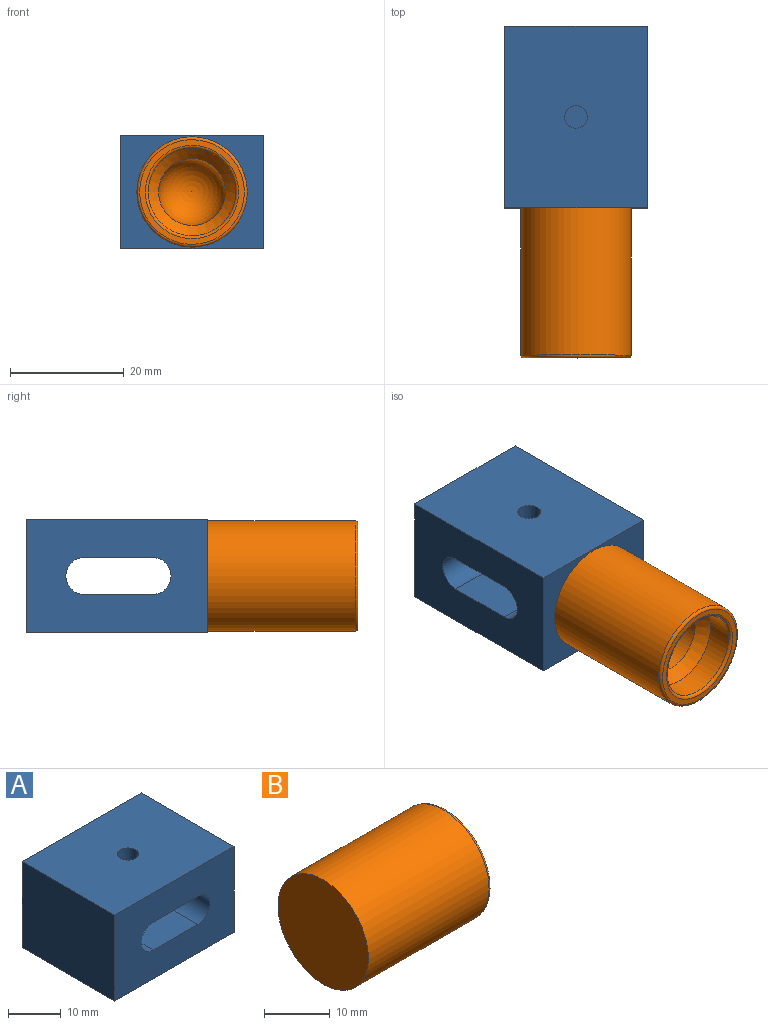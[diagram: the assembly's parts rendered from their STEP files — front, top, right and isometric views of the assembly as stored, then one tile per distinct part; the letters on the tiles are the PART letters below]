
ASSEMBLY  parts=2 mates=1
PART A: 11 faces, bbox 32x25x20 mm
  f0: plane 32x20mm, normal (0,1,0), area 528.8mm2, adj f1,f3,f4,f5,f6,f7,f8,f9
  f1: plane 25x20mm, normal (-1,0,0), area 500mm2, adj f0,f2,f4,f5
  f2: plane 32x20mm, normal (0,-1,0), area 528.8mm2, adj f1,f3,f4,f5,f6,f7,f8,f9
  f3: plane 25x20mm, normal (1,0,0), area 500mm2, adj f0,f2,f4,f5
  f4: plane 32x25mm, normal (0,0,1), area 787.4mm2, adj f0,f1,f2,f3,f10
  f5: plane 32x25mm, normal (0,0,-1), area 800mm2, adj f0,f1,f2,f3
  f6: cylinder r=3.25mm len=25mm, axis (0,-1,0), area 255.3mm2, adj f0,f2,f7,f9
  f7: plane 25x12mm, normal (0,0,1), area 300mm2, adj f0,f2,f6,f8
  f8: cylinder r=3.25mm len=25mm, axis (0,-1,0), area 255.3mm2, adj f0,f2,f7,f9
  f9: plane 25x12mm, normal (0,0,-1), area 287.4mm2, adj f0,f2,f6,f8,f10
  f10: cylinder r=2mm len=6.75mm, axis (0,0,1), area 84.8mm2, adj f4,f9
PART B: 9 faces, bbox 26.4x21x21 mm
  f0: plane 19.4x19.4mm, normal (-1,0,0), area 295.6mm2, adj f8
  f1: sphere r=5.88mm, area 217.2mm2, adj f2
  f2: cylinder r=5.88mm len=11.76mm, axis (-1,0,0), area 406.4mm2, adj f1,f3
  f3: cone r=5.88mm half-angle=42.3deg, axis (1,0,0), area 115.4mm2, adj f2,f4
  f4: cylinder r=7.7mm len=15.4mm, axis (-1,0,0), area 217.7mm2, adj f3,f5
  f5: torus R=8.2mm, axis (-1,0,0), area 38.9mm2, adj f4,f6
  f6: plane 18.4x18.4mm, normal (1,0,0), area 54.7mm2, adj f5,f7
  f7: torus R=9.2mm, axis (-1,0,0), area 47mm2, adj f6,f8
  f8: cylinder r=9.7mm len=25.88mm, axis (-1,0,0), area 1577.3mm2, adj f0,f7
PLACE A rot(axis=(0,0,-1),90deg) t=(-5.12,11.98,-12.54)mm
PLACE B rot(axis=(0.58,-0.58,-0.58),120deg) t=(-5.12,-12.4,-2.54)mm
MATE cylindrical A.f3 <-> B.f2  axis (0,-1,0) through (-5.12,-4.02,-2.54)mm
